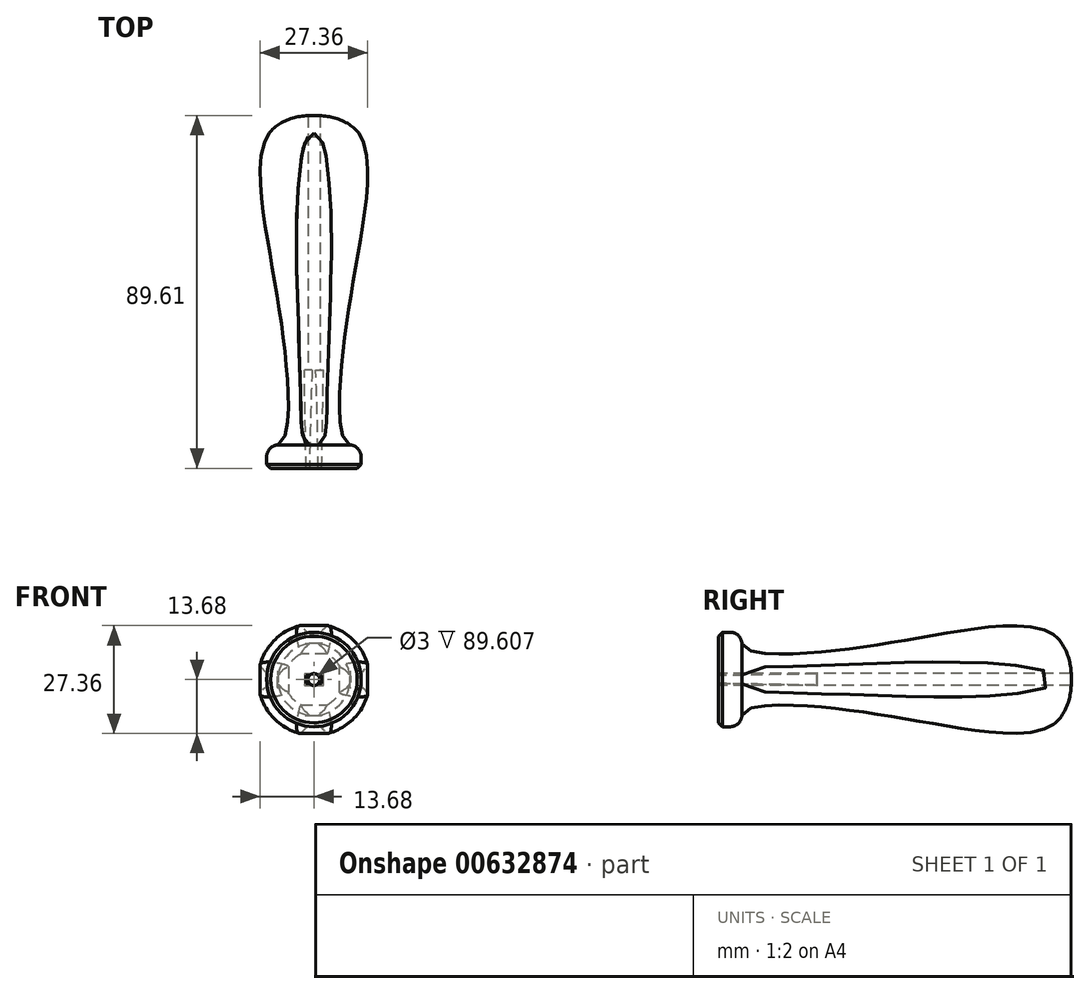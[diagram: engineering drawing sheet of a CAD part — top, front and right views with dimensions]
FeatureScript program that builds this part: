
annotation { "Feature Type Name" : "Feature", "Feature Type Description" : "" }
export const myFeature = defineFeature(function(context is Context, id is Id, definition is map)
    precondition{}
    {
        {
            var Q0;
            Q0=qCreatedBy(makeId("Right.planeOp"),FACE);
            var sketch = newSketch(context, id + "F0", { "sketchPlane" : qUnion([Q0])});
            skLineSegment(sketch, "E0", {"start": v(0, 0) * mm, "end": v(0, 12) * mm});
            skLineSegment(sketch, "E1", {"start": v(0, 12) * mm, "end": v(2.93, 12) * mm});
            skLineSegment(sketch, "E2", {"start": v(81.16, 0) * mm, "end": v(0, 0) * mm});
            skPoint(sketch, "E3.visualSharp", {"position": v(4, 12) * mm});
            skArc(sketch, "E3.filletArc", {"start": v(5.92, 9.15) * mm, "mid": v(5, 11.17) * mm, "end": v(2.93, 12) * mm});
            skFitSpline(sketch, "E4", {"points": [v(5.92, 9.15) * mm, v(36.67, 9.15) * mm, v(83.7, 12.32) * mm, v(89.66, 0) * mm], "startDerivative": vector(8.43, -24.25) * mm, "endDerivative": vector(0, -60.02) * mm});
            skLineSegment(sketch, "E5", {"start": v(81.16, 0) * mm, "end": v(100.7, 0) * mm});
            skFitSpline(sketch, "E6.0", {"points": [v(4.79, 8.76) * mm, v(4.84, 8.61) * mm, v(4.97, 8.34) * mm, v(5.32, 7.87) * mm, v(5.84, 7.45) * mm, v(6.56, 7.08) * mm, v(7.36, 6.8) * mm, v(8.28, 6.58) * mm, v(9.63, 6.34) * mm, v(11.6, 6.15) * mm, v(14.38, 6.07) * mm, v(17.51, 6.11) * mm, v(20.96, 6.27) * mm, v(25.9, 6.64) * mm, v(31.25, 7.2) * mm, v(36.78, 7.94) * mm, v(40.95, 8.57) * mm, v(45.1, 9.25) * mm, v(50.6, 10.18) * mm, v(57.33, 11.32) * mm, v(64.91, 12.42) * mm, v(71.77, 13.04) * mm, v(76.66, 12.96) * mm, v(79.94, 12.45) * mm, v(81.7, 11.94) * mm, v(82.9, 11.4) * mm, v(83.98, 10.8) * mm, v(85.13, 9.88) * mm, v(86.24, 8.56) * mm, v(87.39, 6.55) * mm, v(88.27, 3.64) * mm, v(88.46, 1.19) * mm, v(88.46, 0) * mm]});
            skSolve(sketch);
        }
        {
            var Q0;
            Q0=makeQuery(id+"F0.imprint","IMPRINT",FACE,{"disambiguationData":[TD([[makeQuery(id+"F0.imprint","IMPRINT",EDGE,{"derivedFrom":sQuery(id+"F0.wireOp",EDGE,"E0")}),-1.0]])]});
            var Q1;
            Q1=sQuery(id+"F0.wireOp",EDGE,"E2");
            revolve(context, id + "F1", {"entities" : qUnion([Q0]), "axis" : qUnion([Q1]), "revolveType" : RevolveType.FULL});
        }
        {
            var Q0;
            Q0=makeQuery(id+"F1.opRevolve","SWEPT_EDGE",EDGE,{"disambiguationData":[OSD([sQuery(id+"F0.wireOp",EDGE,"E0"),sQuery(id+"F0.wireOp",EDGE,"E1")])]});
            chamfer(context, id + "F2", {"entities" : qUnion([Q0]), "width" : 1 * mm, "tangentPropagation" : true});
        }
        {
            var Q0;
            Q0=qCreatedBy(makeId("Right.planeOp"),FACE);
            var sketch = newSketch(context, id + "F3", { "sketchPlane" : qUnion([Q0])});
            skLineSegment(sketch, "E7", {"start": v(0, 0) * mm, "end": v(0, 12) * mm});
            skLineSegment(sketch, "E8", {"start": v(81.16, 0) * mm, "end": v(0, 0) * mm});
            skPoint(sketch, "E9.visualSharp", {"position": v(4, 12) * mm});
            skLineSegment(sketch, "E10", {"start": v(81.16, 0) * mm, "end": v(100.7, 0) * mm});
            skFitSpline(sketch, "E11.0", {"points": [v(5.9, 9.16) * mm, v(5.95, 9.01) * mm, v(6.08, 8.74) * mm, v(6.43, 8.28) * mm, v(6.95, 7.85) * mm, v(7.67, 7.48) * mm, v(8.48, 7.2) * mm, v(9.39, 6.99) * mm, v(10.75, 6.76) * mm, v(12.72, 6.57) * mm, v(15.5, 6.5) * mm, v(18.63, 6.55) * mm, v(22.08, 6.72) * mm, v(27.02, 7.1) * mm, v(32.37, 7.68) * mm, v(37.89, 8.44) * mm, v(42.05, 9.08) * mm, v(46.21, 9.77) * mm, v(51.71, 10.71) * mm, v(58.43, 11.87) * mm, v(66, 13) * mm, v(72.86, 13.63) * mm, v(77.76, 13.57) * mm, v(81.03, 13.07) * mm, v(82.79, 12.56) * mm, v(84, 12.04) * mm, v(85.08, 11.43) * mm, v(86.23, 10.52) * mm, v(87.34, 9.2) * mm, v(88.5, 7.2) * mm, v(89.39, 4.3) * mm, v(89.59, 1.83) * mm, v(89.59, 0.65) * mm]});
            skLineSegment(sketch, "E12", {"start": v(5.9, 9.16) * mm, "end": v(9.9, 31.07) * mm});
            skLineSegment(sketch, "E13", {"start": v(9.9, 31.07) * mm, "end": v(93.13, 31.07) * mm});
            skLineSegment(sketch, "E14", {"start": v(93.13, 31.07) * mm, "end": v(87.07, 9.49) * mm});
            skSolve(sketch);
        }
        {
            var Q0;
            Q0=makeQuery(id+"F3.imprint","IMPRINT",FACE,{"disambiguationData":[TD([[makeQuery(id+"F3.imprint","IMPRINT",EDGE,{"derivedFrom":sQuery(id+"F3.wireOp",EDGE,"E11.0")}),1.0]])]});
            extrude(context, id + "F4", {"entities" : qUnion([Q0]), "depth" : 5 * mm, "offsetDistance" : 25 * mm, "hasSecondDirection" : true, "secondDirectionOppositeDirection" : true, "secondDirectionDepth" : 5 * mm});
        }
        {
            var Q0;
            Q0=makeQuery(id+"F4.opExtrude","SWEPT_BODY",BODY,{"disambiguationData":[OSD([sQuery(id+"F3.wireOp",EDGE,"E11.0"),sQuery(id+"F3.wireOp",EDGE,"E12"),sQuery(id+"F3.wireOp",EDGE,"E13"),sQuery(id+"F3.wireOp",EDGE,"E14")])]});
            var Q1;
            {var subQ0=sQuery(id+"F0.wireOp",EDGE,"E0");Q1=makeQuery(id+"F2.opChamfer","BLEND_EDGE",EDGE,{"blendedFrom":[makeQuery(id+"F1.opRevolve","SWEPT_EDGE",EDGE,{"disambiguationData":[OSD([subQ0,sQuery(id+"F0.wireOp",EDGE,"E1")])]}),makeQuery(id+"F1.opRevolve","SWEPT_FACE",FACE,{"disambiguationData":[OSD([subQ0])]})],"blendedInto":[makeQuery(id+"F1.opRevolve","SWEPT_FACE",FACE,{"disambiguationData":[OSD([subQ0])]})]});}
            circularPattern(context, id + "F5", {"entities" : qUnion([Q0]), "axis" : qUnion([Q1]), "angle" : 360 * degree, "instanceCount" : 4, "equalSpace" : true});
        }
        {
            var Q0;
            Q0=makeQuery(id+"F4.opExtrude","SWEPT_BODY",BODY,{"disambiguationData":[OSD([sQuery(id+"F3.wireOp",EDGE,"E11.0"),sQuery(id+"F3.wireOp",EDGE,"E12"),sQuery(id+"F3.wireOp",EDGE,"E13"),sQuery(id+"F3.wireOp",EDGE,"E14")])]});
            var Q1;
            Q1=makeQuery(id+"F5.opPattern","COPY",BODY,{"derivedFrom":makeQuery(id+"F4.opExtrude","SWEPT_BODY",BODY,{"disambiguationData":[OSD([sQuery(id+"F3.wireOp",EDGE,"E11.0"),sQuery(id+"F3.wireOp",EDGE,"E12"),sQuery(id+"F3.wireOp",EDGE,"E13"),sQuery(id+"F3.wireOp",EDGE,"E14")])]}),"instanceName":"1"});
            var Q2;
            Q2=makeQuery(id+"F5.opPattern","COPY",BODY,{"derivedFrom":makeQuery(id+"F4.opExtrude","SWEPT_BODY",BODY,{"disambiguationData":[OSD([sQuery(id+"F3.wireOp",EDGE,"E11.0"),sQuery(id+"F3.wireOp",EDGE,"E12"),sQuery(id+"F3.wireOp",EDGE,"E13"),sQuery(id+"F3.wireOp",EDGE,"E14")])]}),"instanceName":"2"});
            var Q3;
            Q3=makeQuery(id+"F5.opPattern","COPY",BODY,{"derivedFrom":makeQuery(id+"F4.opExtrude","SWEPT_BODY",BODY,{"disambiguationData":[OSD([sQuery(id+"F3.wireOp",EDGE,"E11.0"),sQuery(id+"F3.wireOp",EDGE,"E12"),sQuery(id+"F3.wireOp",EDGE,"E13"),sQuery(id+"F3.wireOp",EDGE,"E14")])]}),"instanceName":"3"});
            var Q4;
            Q4=makeQuery(id+"F1.opRevolve","SWEPT_BODY",BODY,{"disambiguationData":[OSD([sQuery(id+"F0.wireOp",EDGE,"E0"),sQuery(id+"F0.wireOp",EDGE,"E1"),sQuery(id+"F0.wireOp",EDGE,"E2"),sQuery(id+"F0.wireOp",EDGE,"E3.filletArc"),sQuery(id+"F0.wireOp",EDGE,"E4"),sQuery(id+"F0.wireOp",EDGE,"E5")])]});
            booleanBodies(context, id + "F6", {"operationType" : BooleanOperationType.SUBTRACTION, "tools" : qUnion([Q0, Q1, Q2, Q3]), "targets" : qUnion([Q4])});
        }
        {
            var Q0;
            Q0=qCreatedBy(makeId("Front.planeOp"),FACE);
            var sketch = newSketch(context, id + "F7", { "sketchPlane" : qUnion([Q0])});
            skCircle(sketch, "E15", {"center": v(0, 0) * mm, "radius": 1.5 * mm});
            skSolve(sketch);
        }
        {
            var Q0;
            Q0 = qSketchRegion(id + "F7", true);
            extrude(context, id + "F8", {"entities" : qUnion([Q0]), "operationType" : NewBodyOperationType.REMOVE, "oppositeDirection" : true, "depth" : 100 * mm, "offsetDistance" : 25 * mm, "hasSecondDirection" : true, "secondDirectionOppositeDirection" : false, "secondDirectionDepth" : 25 * mm});
        }
        {
            var Q0;
            Q0=qCreatedBy(makeId("Front.planeOp"),FACE);
            var sketch = newSketch(context, id + "F9", { "sketchPlane" : qUnion([Q0])});
            skLineSegment(sketch, "E16.bottom", {"start": v(-2, 1) * mm, "end": v(2, 1) * mm});
            skLineSegment(sketch, "E16.top", {"start": v(-2, -1) * mm, "end": v(2, -1) * mm});
            skLineSegment(sketch, "E16.left", {"start": v(-2, 1) * mm, "end": v(-2, -1) * mm});
            skLineSegment(sketch, "E16.right", {"start": v(2, 1) * mm, "end": v(2, -1) * mm});
            skPoint(sketch, "E16.middle", {"position": v(0, 0) * mm});
            skSolve(sketch);
        }
        {
            var Q0;
            Q0 = qSketchRegion(id + "F9", true);
            extrude(context, id + "F10", {"entities" : qUnion([Q0]), "operationType" : NewBodyOperationType.REMOVE, "oppositeDirection" : true, "depth" : 25 * mm, "offsetDistance" : 25 * mm, "hasDraft" : true, "draftAngle" : 1 * degree});
        }
    });
